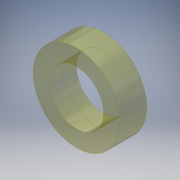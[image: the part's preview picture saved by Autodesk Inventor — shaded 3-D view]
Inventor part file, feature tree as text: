
AUTODESK INVENTOR PART (.ipt)
format: ipt  version: 2019.4 (Build 234330000, 330)  size: 105,472 bytes
history: native  units: mm
features: extrude x1, sketch x1
ambient origin geometry x8: Origin, YZ Plane, XZ Plane, XY Plane, X Axis, Y Axis, Z Axis, Center Point
bodies: Solid1 (feature_tree)
feature tree (2):
  extrude  "Extrusion1"  Depth=2.5mm
  sketch  "Sketch1"  dims[d0=8.0mm d1=5.0mm d2=2.5mm d3=0.0mm]
